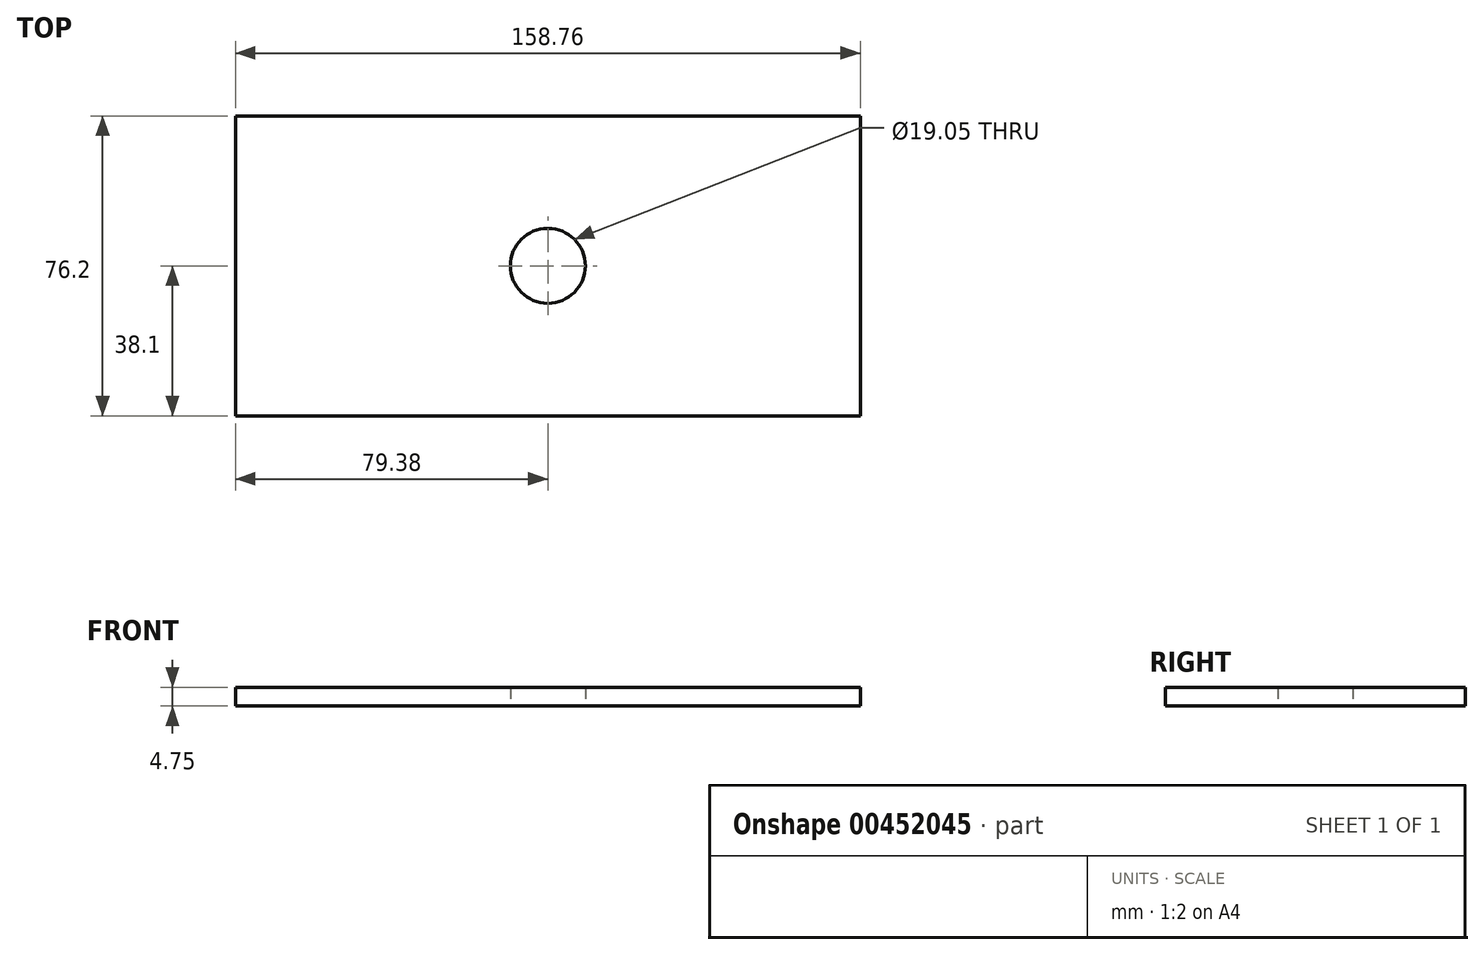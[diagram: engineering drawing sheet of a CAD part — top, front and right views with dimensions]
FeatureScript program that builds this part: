
annotation { "Feature Type Name" : "Feature", "Feature Type Description" : "" }
export const myFeature = defineFeature(function(context is Context, id is Id, definition is map)
    precondition{}
    {
        {
            var Q0;
            Q0=qCreatedBy(makeId("Top.planeOp"),FACE);
            var sketch = newSketch(context, id + "F0", { "sketchPlane" : qUnion([Q0])});
            skLineSegment(sketch, "E0.bottom", {"start": v(79.38, -38.1) * mm, "end": v(-79.38, -38.1) * mm});
            skLineSegment(sketch, "E0.top", {"start": v(79.38, 38.1) * mm, "end": v(-79.38, 38.1) * mm});
            skLineSegment(sketch, "E0.left", {"start": v(79.38, -38.1) * mm, "end": v(79.37, 38.1) * mm});
            skLineSegment(sketch, "E0.right", {"start": v(-79.38, -38.1) * mm, "end": v(-79.38, 38.1) * mm});
            skPoint(sketch, "E0.middle", {"position": v(0, 0) * mm});
            skCircle(sketch, "E1", {"center": v(0, 0) * mm, "radius": 9.53 * mm});
            skSolve(sketch);
        }
        {
            var Q0;
            Q0=makeQuery(id+"F0.imprint","IMPRINT",FACE,{"disambiguationData":[TD([[makeQuery(id+"F0.imprint","IMPRINT",EDGE,{"derivedFrom":sQuery(id+"F0.wireOp",EDGE,"E0.bottom")}),-1.0]])]});
            extrude(context, id + "F1", {"entities" : qUnion([Q0]), "depth" : 4.75 * mm});
        }
    });
